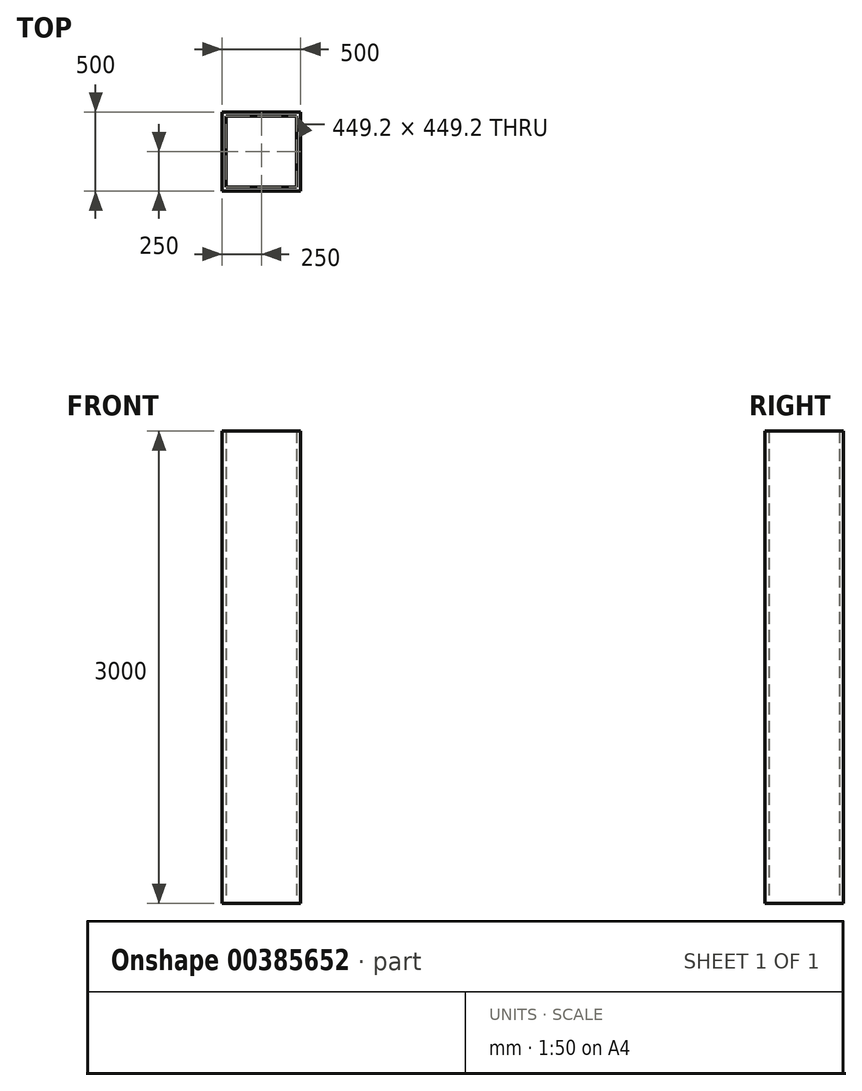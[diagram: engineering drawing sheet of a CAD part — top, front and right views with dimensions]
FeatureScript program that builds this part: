
annotation { "Feature Type Name" : "Feature", "Feature Type Description" : "" }
export const myFeature = defineFeature(function(context is Context, id is Id, definition is map)
    precondition{}
    {
        {
            var Q0;
            Q0=qCreatedBy(makeId("Top.planeOp"),FACE);
            var sketch = newSketch(context, id + "F0", { "sketchPlane" : qUnion([Q0])});
            skLineSegment(sketch, "E0.bottom", {"start": v(-250, 250) * mm, "end": v(250, 250) * mm});
            skLineSegment(sketch, "E0.top", {"start": v(-250, -250) * mm, "end": v(250, -250) * mm});
            skLineSegment(sketch, "E0.left", {"start": v(-250, 250) * mm, "end": v(-250, -250) * mm});
            skLineSegment(sketch, "E0.right", {"start": v(250, 250) * mm, "end": v(250, -250) * mm});
            skLineSegment(sketch, "E1", {"start": v(0, 0) * mm, "end": v(0, 250) * mm, "construction": true});
            skLineSegment(sketch, "E2", {"start": v(0, 0) * mm, "end": v(250, 0) * mm, "construction": true});
            skLineSegment(sketch, "E3.bottom", {"start": v(-224.6, 224.6) * mm, "end": v(224.6, 224.6) * mm});
            skLineSegment(sketch, "E3.top", {"start": v(-224.6, -224.6) * mm, "end": v(224.6, -224.6) * mm});
            skLineSegment(sketch, "E3.left", {"start": v(-224.6, 224.6) * mm, "end": v(-224.6, -224.6) * mm});
            skLineSegment(sketch, "E3.right", {"start": v(224.6, 224.6) * mm, "end": v(224.6, -224.6) * mm});
            skLineSegment(sketch, "E4", {"start": v(0, 0) * mm, "end": v(-224.6, 0) * mm, "construction": true});
            skLineSegment(sketch, "E5", {"start": v(0, 0) * mm, "end": v(0, -224.6) * mm, "construction": true});
            skLineSegment(sketch, "E6", {"start": v(94.53, 224.6) * mm, "end": v(94.53, 0) * mm, "construction": true});
            skSolve(sketch);
        }
        {
            var Q0;
            Q0=makeQuery(id+"F0.imprint","IMPRINT",FACE,{"disambiguationData":[TD([[makeQuery(id+"F0.imprint","IMPRINT",EDGE,{"derivedFrom":sQuery(id+"F0.wireOp",EDGE,"E0.bottom")}),-1.0]])]});
            extrude(context, id + "F1", {"entities" : qUnion([Q0]), "depth" : 3000 * mm});
        }
    });
